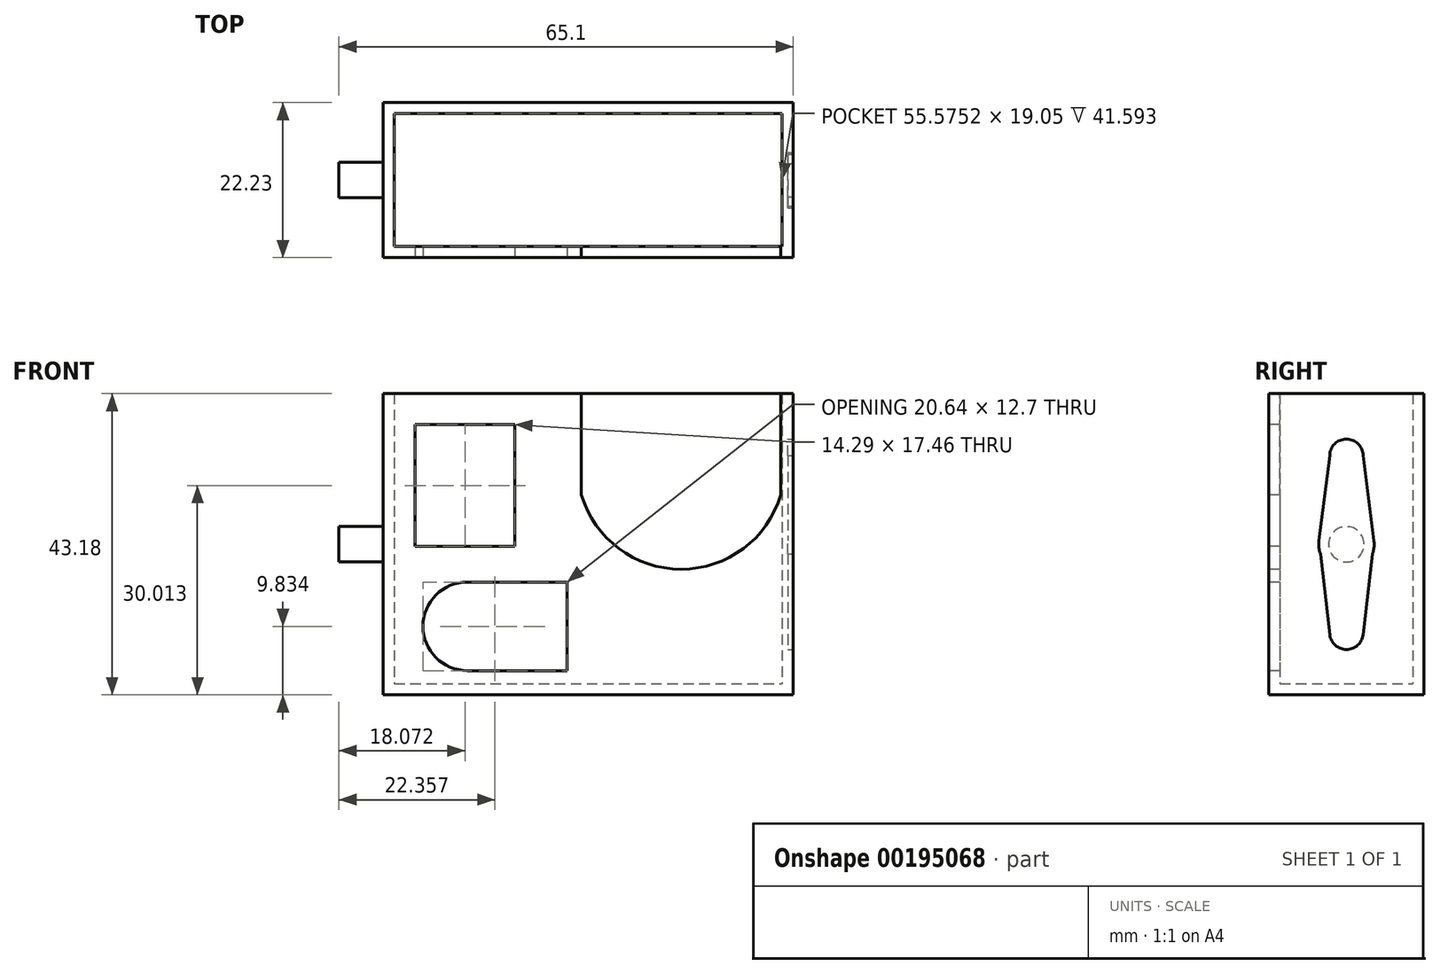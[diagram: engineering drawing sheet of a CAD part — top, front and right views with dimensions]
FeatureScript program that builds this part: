
annotation { "Feature Type Name" : "Feature", "Feature Type Description" : "" }
export const myFeature = defineFeature(function(context is Context, id is Id, definition is map)
    precondition{}
    {
        {
            var Q0;
            Q0=qCreatedBy(makeId("Front.planeOp"),FACE);
            var sketch = newSketch(context, id + "F0", { "sketchPlane" : qUnion([Q0])});
            skLineSegment(sketch, "E0.bottom", {"start": v(-39.77, 11.45) * mm, "end": v(18.98, 11.45) * mm});
            skLineSegment(sketch, "E0.top", {"start": v(-39.77, -31.73) * mm, "end": v(18.98, -31.73) * mm});
            skLineSegment(sketch, "E0.left", {"start": v(-39.77, 11.45) * mm, "end": v(-39.77, -31.73) * mm});
            skLineSegment(sketch, "E0.right", {"start": v(18.98, 11.45) * mm, "end": v(18.98, -31.73) * mm});
            skSolve(sketch);
        }
        {
            var Q0;
            Q0 = qSketchRegion(id + "F0", true);
            extrude(context, id + "F1", {"entities" : qUnion([Q0]), "depth" : 22.22 * mm});
        }
        {
            var Q0;
            Q0=makeQuery(id+"F1.opExtrude","SWEPT_FACE",FACE,{"disambiguationData":[OSD([sQuery(id+"F0.wireOp",EDGE,"E0.bottom")])]});
            shell(context, id + "F2", {"entities" : qUnion([Q0]), "thickness" : 1.59 * mm});
        }
        {
            var Q0;
            Q0=makeQuery(id+"F1.opExtrude","CAP_FACE",FACE,{"disambiguationData":[OSD([sQuery(id+"F0.wireOp",EDGE,"E0.bottom"),sQuery(id+"F0.wireOp",EDGE,"E0.top"),sQuery(id+"F0.wireOp",EDGE,"E0.left"),sQuery(id+"F0.wireOp",EDGE,"E0.right")])],"isStart":false});
            var sketch = newSketch(context, id + "F3", { "sketchPlane" : qUnion([Q0])});
            skLineSegment(sketch, "E1.top", {"start": v(-39.95, -31.4) * mm, "end": v(18.78, -31.4) * mm});
            skLineSegment(sketch, "E1.left", {"start": v(-39.95, 11.78) * mm, "end": v(-39.95, -31.4) * mm});
            skLineSegment(sketch, "E1.right", {"start": v(18.78, 11.78) * mm, "end": v(18.78, -31.4) * mm});
            skLineSegment(sketch, "E2.bottom", {"start": v(-35.2, 7.01) * mm, "end": v(-20.9, 7.01) * mm});
            skLineSegment(sketch, "E2.top", {"start": v(-35.2, -10.45) * mm, "end": v(-20.9, -10.45) * mm});
            skLineSegment(sketch, "E2.left", {"start": v(-35.2, 7.01) * mm, "end": v(-35.2, -10.45) * mm});
            skLineSegment(sketch, "E2.right", {"start": v(-20.9, 7.01) * mm, "end": v(-20.9, -10.45) * mm});
            skLineSegment(sketch, "E3.bottom", {"start": v(-27.73, -15.55) * mm, "end": v(-13.44, -15.55) * mm});
            skLineSegment(sketch, "E3.top", {"start": v(-27.73, -28.25) * mm, "end": v(-13.44, -28.25) * mm});
            skLineSegment(sketch, "E3.right", {"start": v(-13.44, -15.55) * mm, "end": v(-13.44, -28.25) * mm});
            skArc(sketch, "E4", {"start": v(-11.38, -3.05) * mm, "mid": v(2.9, -13.71) * mm, "end": v(17.2, -3.05) * mm});
            skLineSegment(sketch, "E5", {"start": v(-11.38, -3.05) * mm, "end": v(-11.38, 11.78) * mm});
            skLineSegment(sketch, "E6", {"start": v(17.2, -3.05) * mm, "end": v(17.2, 11.78) * mm});
            skLineSegment(sketch, "E7", {"start": v(-39.95, 11.78) * mm, "end": v(-11.38, 11.78) * mm});
            skPoint(sketch, "E8", {"position": v(-34.08, -21.9) * mm});
            skArc(sketch, "E9", {"start": v(-27.73, -15.55) * mm, "mid": v(-34.08, -21.9) * mm, "end": v(-27.73, -28.25) * mm});
            skLineSegment(sketch, "E10", {"start": v(17.2, 11.78) * mm, "end": v(18.78, 11.78) * mm});
            skSolve(sketch);
        }
        {
            var Q0;
            {var subQ0=sQuery(id+"F3.wireOp",EDGE,"E4");Q0=makeQuery(id+"F3.imprint","IMPRINT",FACE,{"disambiguationData":[TD([[makeQuery(id+"F3.imprint","IMPRINT",EDGE,{"derivedFrom":subQ0}),1.0]])]});}
            var Q1;
            Q1=makeQuery(id+"F3.imprint","IMPRINT",FACE,{"disambiguationData":[TD([[makeQuery(id+"F3.imprint","IMPRINT",EDGE,{"derivedFrom":sQuery(id+"F3.wireOp",EDGE,"E2.bottom")}),-1.0]])]});
            var Q2;
            Q2=makeQuery(id+"F3.imprint","IMPRINT",FACE,{"disambiguationData":[TD([[makeQuery(id+"F3.imprint","IMPRINT",EDGE,{"derivedFrom":sQuery(id+"F3.wireOp",EDGE,"E3.bottom")}),-1.0]])]});
            extrude(context, id + "F4", {"entities" : qUnion([Q0, Q1, Q2]), "operationType" : NewBodyOperationType.REMOVE, "oppositeDirection" : true, "depth" : 3.17 * mm});
        }
        {
            var Q0;
            Q0=makeQuery(id+"F1.opExtrude","SWEPT_FACE",FACE,{"disambiguationData":[OSD([sQuery(id+"F0.wireOp",EDGE,"E0.right")])]});
            var sketch = newSketch(context, id + "F5", { "sketchPlane" : qUnion([Q0])});
            skCircle(sketch, "E11", {"center": v(-11.11, -10.14) * mm, "radius": 3.97 * mm});
            skPoint(sketch, "E12", {"position": v(-11.11, 2.56) * mm});
            skCircle(sketch, "E13", {"center": v(-11.11, 2.56) * mm, "radius": 2.38 * mm});
            skLineSegment(sketch, "E14", {"start": v(-13.5, 2.56) * mm, "end": v(-15.05, -9.64) * mm});
            skLineSegment(sketch, "E15", {"start": v(-8.73, 2.56) * mm, "end": v(-7.18, -9.64) * mm});
            skPoint(sketch, "E16", {"position": v(-11.11, -22.84) * mm});
            skPoint(sketch, "E16.positionSnap0", {"position": v(-11.11, -31.73) * mm});
            skCircle(sketch, "E17", {"center": v(-11.11, -22.84) * mm, "radius": 2.39 * mm});
            skLineSegment(sketch, "E18", {"start": v(-15.05, -9.64) * mm, "end": v(-13.48, -23.11) * mm});
            skLineSegment(sketch, "E19", {"start": v(-7.18, -9.64) * mm, "end": v(-8.74, -23.11) * mm});
            skSolve(sketch);
        }
        {
            var Q0;
            Q0 = qSketchRegion(id + "F5", true);
            extrude(context, id + "F6", {"entities" : qUnion([Q0]), "operationType" : NewBodyOperationType.REMOVE, "oppositeDirection" : true, "depth" : 0.8 * mm});
        }
        {
            var Q0;
            Q0=makeQuery(id+"F1.opExtrude","SWEPT_FACE",FACE,{"disambiguationData":[OSD([sQuery(id+"F0.wireOp",EDGE,"E0.left")])]});
            var sketch = newSketch(context, id + "F7", { "sketchPlane" : qUnion([Q0])});
            skCircle(sketch, "E20", {"center": v(11.11, -10.14) * mm, "radius": 2.54 * mm});
            skSolve(sketch);
        }
        {
            var Q0;
            Q0 = qSketchRegion(id + "F7", true);
            extrude(context, id + "F8", {"entities" : qUnion([Q0]), "operationType" : NewBodyOperationType.ADD, "depth" : 6.35 * mm});
        }
    });
